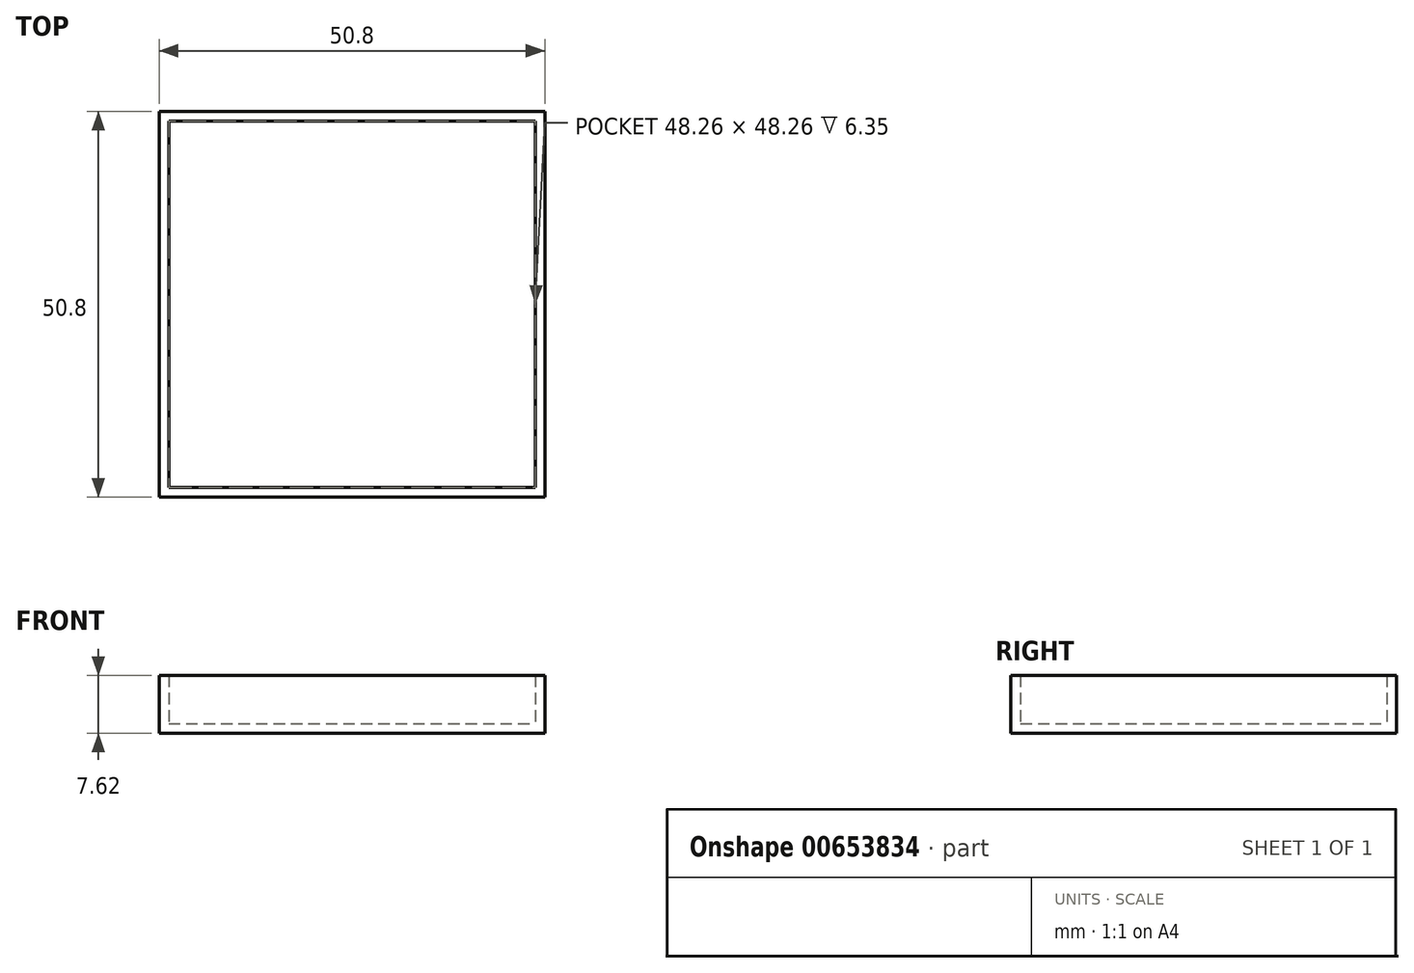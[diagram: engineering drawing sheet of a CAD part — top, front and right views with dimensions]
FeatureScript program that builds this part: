
annotation { "Feature Type Name" : "Feature", "Feature Type Description" : "" }
export const myFeature = defineFeature(function(context is Context, id is Id, definition is map)
    precondition{}
    {
        {
            var Q0;
            Q0=qCreatedBy(makeId("Top.planeOp"),FACE);
            var sketch = newSketch(context, id + "F0", { "sketchPlane" : qUnion([Q0])});
            skLineSegment(sketch, "E0", {"start": v(0, 0) * mm, "end": v(0, 50.8) * mm});
            skLineSegment(sketch, "E1", {"start": v(0, 50.8) * mm, "end": v(50.8, 50.8) * mm});
            skLineSegment(sketch, "E2", {"start": v(50.8, 50.8) * mm, "end": v(50.8, 0) * mm});
            skLineSegment(sketch, "E3", {"start": v(0, 0) * mm, "end": v(50.8, 0) * mm});
            skSolve(sketch);
        }
        {
            var Q0;
            Q0=makeQuery(id+"F0.imprint","IMPRINT",FACE,{"disambiguationData":[TD([[makeQuery(id+"F0.imprint","IMPRINT",EDGE,{"derivedFrom":sQuery(id+"F0.wireOp",EDGE,"E0")}),-1.0]])]});
            extrude(context, id + "F1", {"entities" : qUnion([Q0]), "depth" : 7.62 * mm, "offsetDistance" : 25.4 * mm});
        }
        {
            var Q0;
            Q0=makeQuery(id+"F1.opExtrude","CAP_FACE",FACE,{"disambiguationData":[OSD([sQuery(id+"F0.wireOp",EDGE,"E0"),sQuery(id+"F0.wireOp",EDGE,"E1"),sQuery(id+"F0.wireOp",EDGE,"E2"),sQuery(id+"F0.wireOp",EDGE,"E3")])],"isStart":false});
            shell(context, id + "F2", {"entities" : qUnion([Q0]), "thickness" : 1.27 * mm});
        }
    });
